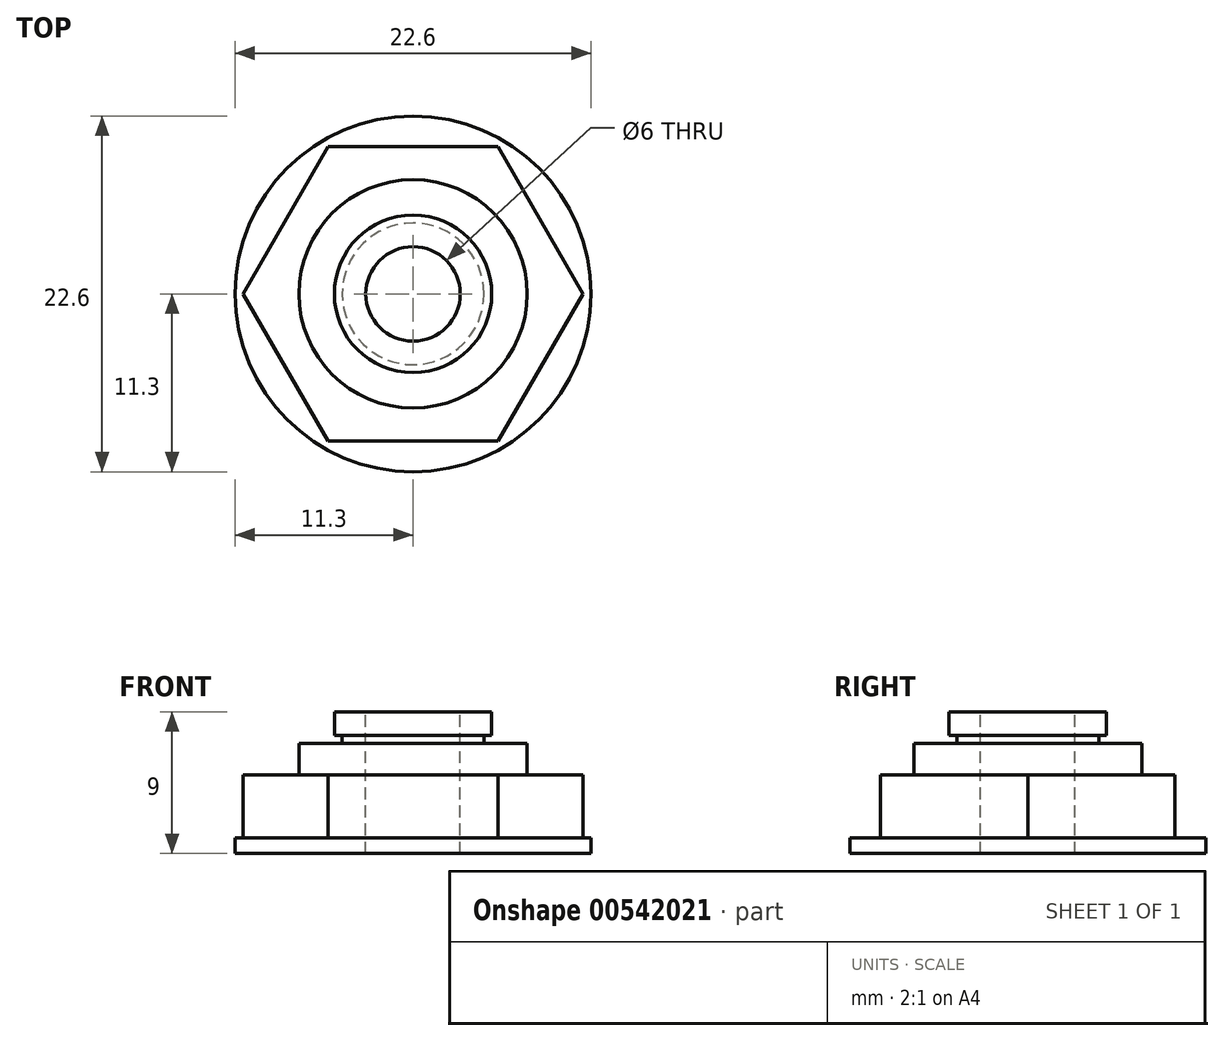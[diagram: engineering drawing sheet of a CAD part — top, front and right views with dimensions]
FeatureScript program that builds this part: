
annotation { "Feature Type Name" : "Feature", "Feature Type Description" : "" }
export const myFeature = defineFeature(function(context is Context, id is Id, definition is map)
    precondition{}
    {
        {
            var Q0;
            Q0=qCreatedBy(makeId("Top.planeOp"),FACE);
            var sketch = newSketch(context, id + "F0", { "sketchPlane" : qUnion([Q0])});
            skCircle(sketch, "E0", {"center": v(0, 0) * mm, "radius": 11.3 * mm});
            skCircle(sketch, "E1.cCircle", {"center": v(0, 0) * mm, "radius": 10.8 * mm, "construction": true});
            skLineSegment(sketch, "E1.0", {"start": v(5.4, -9.35) * mm, "end": v(-5.4, -9.35) * mm});
            skLineSegment(sketch, "E1.1", {"start": v(-5.4, -9.35) * mm, "end": v(-10.8, 0) * mm});
            skLineSegment(sketch, "E1.2", {"start": v(-10.8, 0) * mm, "end": v(-5.4, 9.35) * mm});
            skLineSegment(sketch, "E1.3", {"start": v(-5.4, 9.35) * mm, "end": v(5.4, 9.35) * mm});
            skLineSegment(sketch, "E1.4", {"start": v(5.4, 9.35) * mm, "end": v(10.8, 0) * mm});
            skLineSegment(sketch, "E1.5", {"start": v(10.8, 0) * mm, "end": v(5.4, -9.35) * mm});
            skSolve(sketch);
        }
        {
            var Q0;
            Q0=makeQuery(id+"F0.imprint","IMPRINT",FACE,{"disambiguationData":[TD([[makeQuery(id+"F0.imprint","IMPRINT",EDGE,{"derivedFrom":sQuery(id+"F0.wireOp",EDGE,"E0")}),1.0]])]});
            var Q1;
            Q1=makeQuery(id+"F0.imprint","IMPRINT",FACE,{"disambiguationData":[TD([[makeQuery(id+"F0.imprint","IMPRINT",EDGE,{"derivedFrom":sQuery(id+"F0.wireOp",EDGE,"E1.0")}),-1.0]])]});
            extrude(context, id + "F1", {"entities" : qUnion([Q0, Q1]), "depth" : 1 * mm});
        }
        {
            var Q0;
            Q0=makeQuery(id+"F0.imprint","IMPRINT",FACE,{"disambiguationData":[TD([[makeQuery(id+"F0.imprint","IMPRINT",EDGE,{"derivedFrom":sQuery(id+"F0.wireOp",EDGE,"E1.0")}),-1.0]])]});
            extrude(context, id + "F2", {"entities" : qUnion([Q0]), "operationType" : NewBodyOperationType.ADD, "depth" : 5 * mm});
        }
        {
            var Q0;
            Q0=makeQuery(id+"F2.opExtrude","CAP_FACE",FACE,{"disambiguationData":[OSD([sQuery(id+"F0.wireOp",EDGE,"E1.0"),sQuery(id+"F0.wireOp",EDGE,"E1.1"),sQuery(id+"F0.wireOp",EDGE,"E1.2"),sQuery(id+"F0.wireOp",EDGE,"E1.3"),sQuery(id+"F0.wireOp",EDGE,"E1.4"),sQuery(id+"F0.wireOp",EDGE,"E1.5")])],"isStart":false});
            var sketch = newSketch(context, id + "F3", { "sketchPlane" : qUnion([Q0])});
            skCircle(sketch, "E2", {"center": v(0, 0) * mm, "radius": 7.25 * mm});
            skSolve(sketch);
        }
        {
            var Q0;
            Q0=qSketchRegion(id+"F3",true);
            extrude(context, id + "F4", {"entities" : qUnion([Q0]), "operationType" : NewBodyOperationType.ADD, "depth" : 2 * mm});
        }
        {
            var Q0;
            Q0=makeQuery(id+"F4.opExtrude","CAP_FACE",FACE,{"disambiguationData":[OSD([sQuery(id+"F3.wireOp",EDGE,"E2")])],"isStart":false});
            var sketch = newSketch(context, id + "F5", { "sketchPlane" : qUnion([Q0])});
            skCircle(sketch, "E3", {"center": v(0, 0) * mm, "radius": 4.5 * mm});
            skSolve(sketch);
        }
        {
            var Q0;
            Q0=qSketchRegion(id+"F5",true);
            extrude(context, id + "F6", {"entities" : qUnion([Q0]), "operationType" : NewBodyOperationType.ADD, "depth" : .5 * mm});
        }
        {
            var Q0;
            Q0=makeQuery(id+"F6.opExtrude","CAP_FACE",FACE,{"disambiguationData":[OSD([sQuery(id+"F5.wireOp",EDGE,"E3")])],"isStart":false});
            var sketch = newSketch(context, id + "F7", { "sketchPlane" : qUnion([Q0])});
            skCircle(sketch, "E4", {"center": v(0, 0) * mm, "radius": 5 * mm});
            skSolve(sketch);
        }
        {
            var Q0;
            Q0=qSketchRegion(id+"F7",true);
            extrude(context, id + "F8", {"entities" : qUnion([Q0]), "operationType" : NewBodyOperationType.ADD, "depth" : 1.5 * mm});
        }
        {
            var Q0;
            Q0=makeQuery(id+"F8.opExtrude","CAP_FACE",FACE,{"disambiguationData":[OSD([sQuery(id+"F7.wireOp",EDGE,"E4")])],"isStart":false});
            var sketch = newSketch(context, id + "F9", { "sketchPlane" : qUnion([Q0])});
            skCircle(sketch, "E5", {"center": v(0, 0) * mm, "radius": 3 * mm});
            skSolve(sketch);
        }
        {
            var Q0;
            Q0=qSketchRegion(id+"F9",true);
            extrude(context, id + "F10", {"entities" : qUnion([Q0]), "operationType" : NewBodyOperationType.REMOVE, "oppositeDirection" : true, "depth" : 13.7 * mm});
        }
    });
